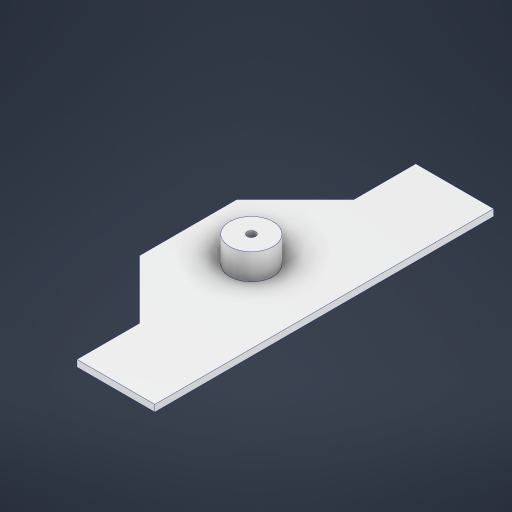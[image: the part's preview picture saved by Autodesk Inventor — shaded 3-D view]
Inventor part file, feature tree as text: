
AUTODESK INVENTOR PART (.ipt)
format: ipt  version: 2024 (Build 280153000, 153)  size: 207,360 bytes
history: native  units: mm
features: extrude x2, sketch x2
ambient origin geometry x8: Origin, YZ Plane, XZ Plane, XY Plane, X Axis, Y Axis, Z Axis, Center Point
bodies: Solid1 (feature_tree)
feature tree (4):
  extrude  "Extrusion1"  Depth=117.0mm
  extrude  "Extrusion2"  Depth=39.0mm
  sketch  "Sketch1"  dims[d0=509.0mm d1=117.0mm]
  sketch  "Sketch2"  dims[d2=117.0mm d3=93.0mm d4=94.0mm d6=88.0mm d7=88.0mm d8=88.0mm d9=88.0mm d10=10.0mm d11=0.0mm d12=39.0mm d13=0.0mm d14=95.0mm d16=254.0mm d17=110.0mm d18=65.0mm d19=12.5mm]
